# Revit family: Drain_Trap_Deep-Seal-Zurn-Z1000
name_source: partatom
category: Plumbing Fixtures
units: mm (PartAtom-declared; Revit-internal decimal feet)

## family parameters
Always vertical = Yes
Cut with Voids When Loaded = No
Maintain Annotation Orientation = No
OmniClass Number = 23.45.55.21
OmniClass Title = Drains (Wastes)
Part Type = Normal
Room Calculation Point = No
Round Connector Dimension = Use Radius
Shared = No
Work Plane-Based = No

## types (6) — shared parameters
CW Connection = No
Default Elevation = 20 "
Description = DEEP SEAL TRAP
HW Connection = No
Main Material = Iron - Zurn - Cast - Painted - Blue
Manufacturer = Zurn Water, LLC
Manufacurer Brand = Zurn
Model = Z1000
Modified Date = 02/27/2026
Plug Material = Bronze - Zurn - Polished
Product Documentation Link = https://files.zurn.com
Product Installation Sheet URL = https://files.zurn.com
Product Page URL = https://www.zurn.com
Product data url = https://www.bimobject.com
URL = www.zurn.com
Vent Connection = No
WFU = 1
Waste Connection = Yes
zero-valued in all types: CWFU, HWFU

## per-type parameters (varying)
| type | Approx. Weight (Lbs) | Assembly Code | Bend Radius | Cleanout Loc. | Connector Radius | Dim 'B' | Dim 'C' | Dim 'D' | Dim 'E' | Outlet Length | Pipe Size 'A' (Inner Diameter) | Pipe Size 'A' (Inner Radius) | Pipe Size 'A' (Nominal Diameter) | Pipe Size 'A' (Outer Diameter) | Pipe Size 'A' (Outer Radius) | Plug Radius | Threaded Outlet |
| Z1000 - 3 Inch No-Hub Outlet | 32.00 lbf | D2040200 | 2.5 " | 1.825 " | 1.5 " | 13.5 " | 5 " | 8 " | 3.5 " | 1.41 " | 3.068 " | 1.534 " | 3 " | 3.5 " | 1.75 " | 1.125 " | No |
| Z1000 - 2 Inch No-Hub Outlet | 8.00 lbf | D2040200 | 1.375 " | 1.969 " | 1 " | 10.5 " | 4 " | 6.5 " | 2.75 " | 1.188 " | 2.067 " | 1.034 " | 2 " | 2.275 " | 1.138 " | 1 " | No |
| Z1000 - 4 Inch No-Hub Outlet | 32.00 lbf | D2040200 | 2.5 " | 2.795 " | 2 " | 15.25 " | 5 " | 9.5 " | 4.25 " | 1.41 " | 4.028 " | 2.014 " | 4 " | 4.5 " | 2.25 " | 1.75 " | No |
| Z1000 - 2 Inch IP Threaded Outlet | 8.00 lbf | D2040200 | 1.375 " | 1.75 " | 1 " | 9.5 " | 4 " | 5.875 " | 1.75 " | 1 " | 2.067 " | 1.034 " | 2 " | 2.275 " | 1.138 " | 1 " | Yes |
| Z1000 - 3 Inch IP Threaded Outlet | 17.00 lbf | D2040200 | 2.5 " | 1.825 " | 1.5 " | 13 " | 5 " | 7.5 " | 3 " | 1.35 " | 3.026 " | 1.513 " | 3 " | 3.5 " | 1.75 " | 1.125 " | Yes |
| Z1000 - 4 Inch IP Threaded Outlet | 32.00 lbf | D2040100 | 2.5 " | 2.795 " | 2 " | 15 " | 5 " | 9.5 " | 4 " | 1.41 " | 4.026 " | 2.013 " | 4 " | 4.5 " | 2.25 " | 1.75 " | Yes |

## geometry (parser evidence)
native form markers: Blend x6, Sweep x2
no freeform markers — native parametric forms only
